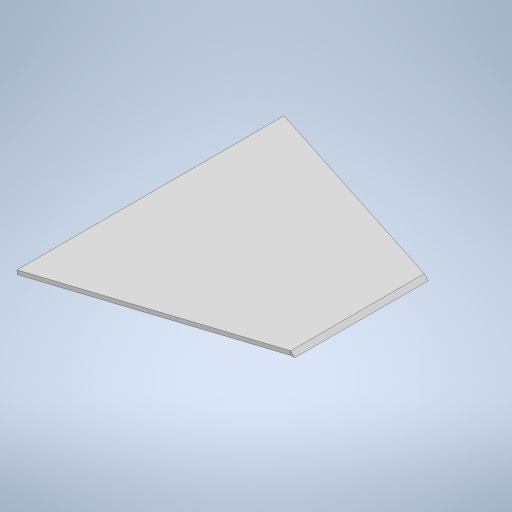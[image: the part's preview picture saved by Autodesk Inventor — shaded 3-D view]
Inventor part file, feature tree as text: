
AUTODESK INVENTOR PART (.ipt)
format: ipt  version: 2024.3 (Build 283343000, 343)  size: 223,232 bytes
history: native  units: mm
features: extrude x2, sketch x2
ambient origin geometry x8: Origin, YZ Plane, XZ Plane, XY Plane, X Axis, Y Axis, Z Axis, Center Point
bodies: Solid1 (feature_tree)
feature tree (4):
  extrude  "Extrusion1"  Depth=200.0mm
  extrude  "Extrusion2"  Depth=100.0mm
  sketch  "Sketch1"  dims[d0=155.0mm d1=200.0mm]
  sketch  "Sketch2"  dims[d2=50.0mm d3=50.0mm d4=3.0mm d5=0.0mm d6=45.0deg d7=100.0mm d8=0.0mm]
